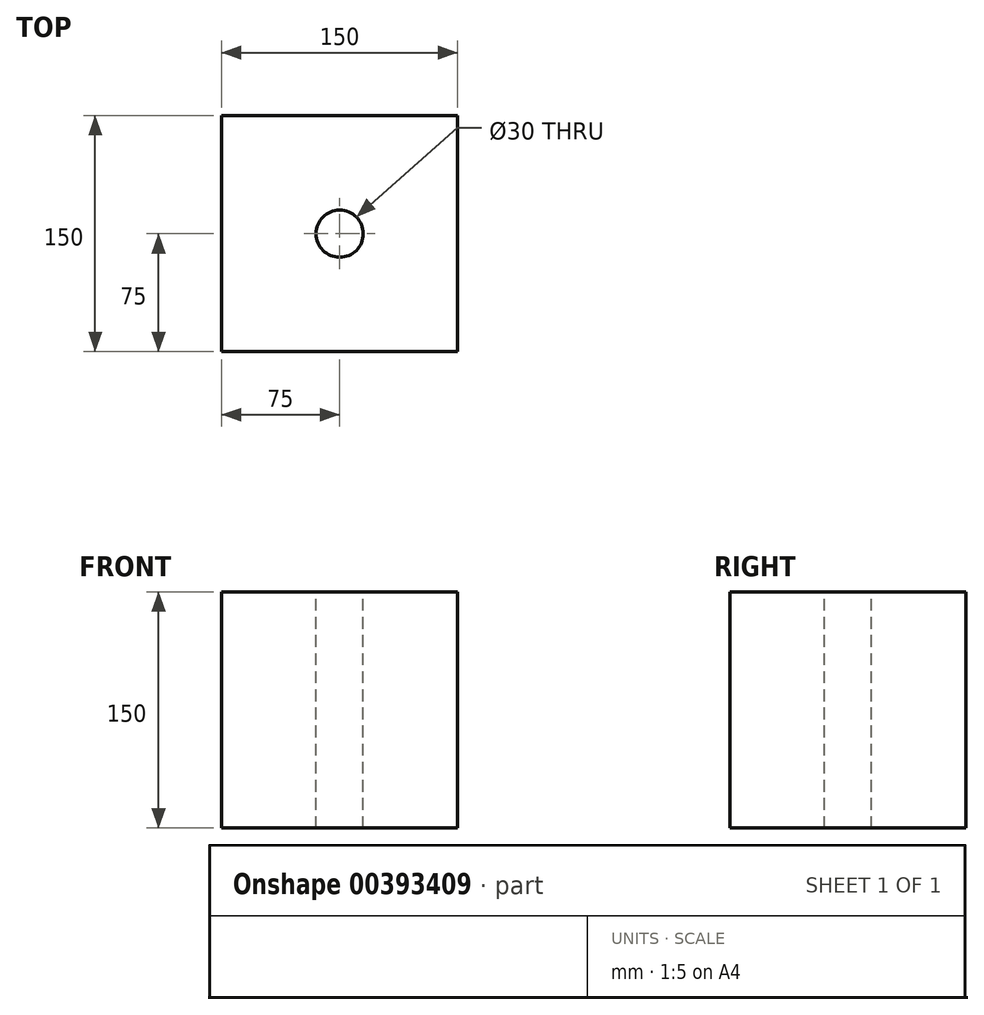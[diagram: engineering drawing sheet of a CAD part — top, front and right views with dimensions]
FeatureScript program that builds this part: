
annotation { "Feature Type Name" : "Feature", "Feature Type Description" : "" }
export const myFeature = defineFeature(function(context is Context, id is Id, definition is map)
    precondition{}
    {
        {
            var Q0;
            Q0=qCreatedBy(makeId("Front.planeOp"),FACE);
            var sketch = newSketch(context, id + "F0", { "sketchPlane" : qUnion([Q0])});
            skLineSegment(sketch, "E0.bottom", {"start": v(75, 75) * mm, "end": v(-75, 75) * mm});
            skLineSegment(sketch, "E0.top", {"start": v(75, -75) * mm, "end": v(-75, -75) * mm});
            skLineSegment(sketch, "E0.left", {"start": v(75, 75) * mm, "end": v(75, -75) * mm});
            skLineSegment(sketch, "E0.right", {"start": v(-75, 75) * mm, "end": v(-75, -75) * mm});
            skPoint(sketch, "E0.middle", {"position": v(0, 0) * mm});
            skSolve(sketch);
        }
        {
            var Q0;
            Q0 = qSketchRegion(id + "F0", true);
            extrude(context, id + "F1", {"entities" : qUnion([Q0]), "depth" : 150 * mm});
        }
        {
            var Q0;
            Q0=makeQuery(id+"F1.opExtrude","SWEPT_FACE",FACE,{"disambiguationData":[OSD([sQuery(id+"F0.wireOp",EDGE,"E0.bottom")])]});
            var sketch = newSketch(context, id + "F2", { "sketchPlane" : qUnion([Q0])});
            skCircle(sketch, "E1", {"center": v(0, -75) * mm, "radius": 15 * mm});
            skPoint(sketch, "E1.centerSnap0", {"position": v(-75, -75) * mm});
            skSolve(sketch);
        }
        {
            var Q0;
            Q0 = qSketchRegion(id + "F2", true);
            extrude(context, id + "F3", {"entities" : qUnion([Q0]), "operationType" : NewBodyOperationType.REMOVE, "oppositeDirection" : true, "depth" : 150 * mm});
        }
    });
